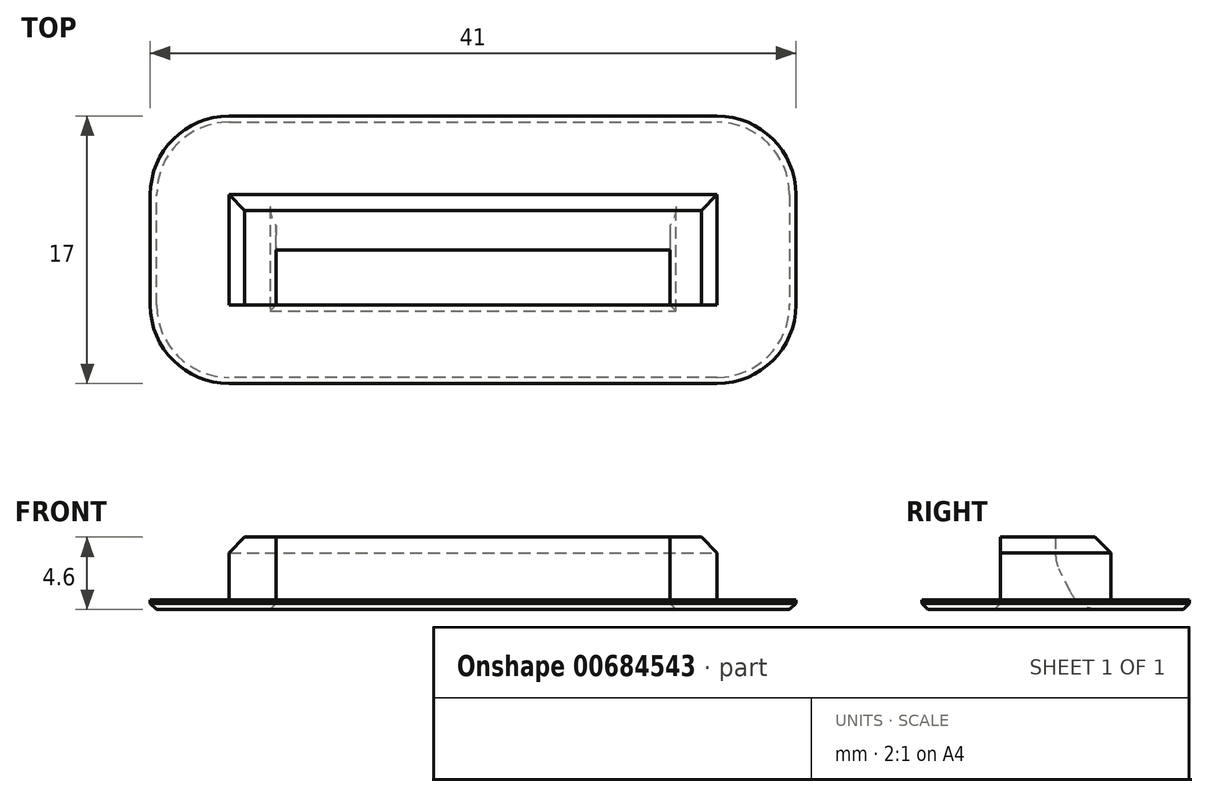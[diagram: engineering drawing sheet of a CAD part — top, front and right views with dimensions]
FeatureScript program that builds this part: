
annotation { "Feature Type Name" : "Feature", "Feature Type Description" : "" }
export const myFeature = defineFeature(function(context is Context, id is Id, definition is map)
    precondition{}
    {
        {
            var Q0;
            Q0=qCreatedBy(makeId("Top.planeOp"),FACE);
            var sketch = newSketch(context, id + "F0", { "sketchPlane" : qUnion([Q0])});
            skLineSegment(sketch, "E0.bottom", {"start": v(5, 0) * mm, "end": v(36, 0) * mm});
            skLineSegment(sketch, "E0.top", {"start": v(5, 17) * mm, "end": v(36, 17) * mm});
            skLineSegment(sketch, "E0.left", {"start": v(0, 5) * mm, "end": v(0, 12) * mm});
            skLineSegment(sketch, "E0.right", {"start": v(41, 5) * mm, "end": v(41, 12) * mm});
            skLineSegment(sketch, "E1.bottom", {"start": v(8, 0) * mm, "end": v(33, 0) * mm});
            skLineSegment(sketch, "E1.top", {"start": v(8, 8.5) * mm, "end": v(33, 8.5) * mm});
            skLineSegment(sketch, "E1.left", {"start": v(8, 0) * mm, "end": v(8, 8.5) * mm});
            skLineSegment(sketch, "E1.right", {"start": v(33, 0) * mm, "end": v(33, 8.5) * mm});
            skPoint(sketch, "E2.visualSharp", {"position": v(0, 17) * mm});
            skArc(sketch, "E2.filletArc", {"start": v(5, 17) * mm, "mid": v(1.46, 15.54) * mm, "end": v(0, 12) * mm});
            skPoint(sketch, "E3.visualSharp", {"position": v(0, 0) * mm});
            skArc(sketch, "E3.filletArc", {"start": v(0, 5) * mm, "mid": v(1.46, 1.46) * mm, "end": v(5, 0) * mm});
            skPoint(sketch, "E4.visualSharp", {"position": v(41, 17) * mm});
            skArc(sketch, "E4.filletArc", {"start": v(41, 12) * mm, "mid": v(39.54, 15.54) * mm, "end": v(36, 17) * mm});
            skPoint(sketch, "E5.visualSharp", {"position": v(41, 0) * mm});
            skArc(sketch, "E5.filletArc", {"start": v(36, 0) * mm, "mid": v(39.54, 1.46) * mm, "end": v(41, 5) * mm});
            skSolve(sketch);
        }
        {
            var Q0;
            Q0=makeQuery(id+"F0.imprint","IMPRINT",FACE,{"disambiguationData":[TD([[makeQuery(id+"F0.imprint","IMPRINT",EDGE,{"derivedFrom":sQuery(id+"F0.wireOp",EDGE,"E0.top")}),-1.0]])]});
            extrude(context, id + "F1", {"entities" : qUnion([Q0]), "depth" : 0.6 * mm, "offsetDistance" : 25 * mm});
        }
        {
            var Q0;
            Q0=makeQuery(id+"F1.opExtrude","CAP_FACE",FACE,{"disambiguationData":[OSD([sQuery(id+"F0.wireOp",EDGE,"E0.bottom"),sQuery(id+"F0.wireOp",EDGE,"E0.top"),sQuery(id+"F0.wireOp",EDGE,"E0.left"),sQuery(id+"F0.wireOp",EDGE,"E0.right"),sQuery(id+"F0.wireOp",EDGE,"E1.top"),sQuery(id+"F0.wireOp",EDGE,"E1.left"),sQuery(id+"F0.wireOp",EDGE,"E1.right"),sQuery(id+"F0.wireOp",EDGE,"E2.filletArc"),sQuery(id+"F0.wireOp",EDGE,"E3.filletArc"),sQuery(id+"F0.wireOp",EDGE,"E4.filletArc"),sQuery(id+"F0.wireOp",EDGE,"E5.filletArc")])],"isStart":false});
            var sketch = newSketch(context, id + "F2", { "sketchPlane" : qUnion([Q0])});
            skLineSegment(sketch, "E6.bottom", {"start": v(5, 12) * mm, "end": v(36, 12) * mm});
            skLineSegment(sketch, "E6.top", {"start": v(5, 5) * mm, "end": v(36, 5) * mm});
            skLineSegment(sketch, "E6.left", {"start": v(5, 12) * mm, "end": v(5, 5) * mm});
            skLineSegment(sketch, "E6.right", {"start": v(36, 12) * mm, "end": v(36, 5) * mm});
            skSolve(sketch);
        }
        {
            var Q0;
            Q0=makeQuery(id+"F2.imprint","IMPRINT",FACE,{"disambiguationData":[TD([[makeQuery(id+"F2.imprint","IMPRINT",EDGE,{"derivedFrom":sQuery(id+"F2.wireOp",EDGE,"E6.bottom")}),-1.0]])]});
            extrude(context, id + "F3", {"entities" : qUnion([Q0]), "operationType" : NewBodyOperationType.ADD, "depth" : 4 * mm, "offsetDistance" : 25 * mm});
        }
        {
            var Q0;
            Q0=makeQuery(id+"F3.opExtrude","CAP_EDGE",EDGE,{"disambiguationData":[OSD([sQuery(id+"F2.wireOp",EDGE,"E6.left")])],"isStart":false});
            var Q1;
            Q1=makeQuery(id+"F3.opExtrude","CAP_EDGE",EDGE,{"disambiguationData":[OSD([sQuery(id+"F2.wireOp",EDGE,"E6.bottom")])],"isStart":false});
            var Q2;
            Q2=makeQuery(id+"F3.opExtrude","CAP_EDGE",EDGE,{"disambiguationData":[OSD([sQuery(id+"F2.wireOp",EDGE,"E6.right")])],"isStart":false});
            chamfer(context, id + "F4", {"entities" : qUnion([Q0, Q1, Q2]), "width" : 1 * mm, "tangentPropagation" : true});
        }
        {
            var Q0;
            Q0=makeQuery(id+"F1.opExtrude","CAP_EDGE",EDGE,{"disambiguationData":[OSD([sQuery(id+"F0.wireOp",EDGE,"E1.top")])],"isStart":true});
            chamfer(context, id + "F5", {"entities" : qUnion([Q0]), "chamferType" : ChamferType.TWO_OFFSETS, "width1" : 3 * mm, "oppositeDirection" : false, "width2" : 1.5 * mm, "tangentPropagation" : true});
        }
        {
            var Q0;
            {var subQ0=sQuery(id+"F0.wireOp",EDGE,"E1.top");Q0=makeQuery(id+"F5.opChamfer","BLEND_EDGE",EDGE,{"blendedFrom":[makeQuery(id+"F1.opExtrude","CAP_EDGE",EDGE,{"disambiguationData":[OSD([subQ0])],"isStart":true}),makeQuery(id+"F1.opExtrude","CAP_FACE",FACE,{"disambiguationData":[OSD([sQuery(id+"F0.wireOp",EDGE,"E0.bottom"),sQuery(id+"F0.wireOp",EDGE,"E0.top"),sQuery(id+"F0.wireOp",EDGE,"E0.left"),sQuery(id+"F0.wireOp",EDGE,"E0.right"),subQ0,sQuery(id+"F0.wireOp",EDGE,"E1.left"),sQuery(id+"F0.wireOp",EDGE,"E1.right"),sQuery(id+"F0.wireOp",EDGE,"E2.filletArc"),sQuery(id+"F0.wireOp",EDGE,"E3.filletArc"),sQuery(id+"F0.wireOp",EDGE,"E4.filletArc"),sQuery(id+"F0.wireOp",EDGE,"E5.filletArc")])],"isStart":true})],"blendedInto":[makeQuery(id+"F1.opExtrude","CAP_FACE",FACE,{"disambiguationData":[OSD([sQuery(id+"F0.wireOp",EDGE,"E0.bottom"),sQuery(id+"F0.wireOp",EDGE,"E0.top"),sQuery(id+"F0.wireOp",EDGE,"E0.left"),sQuery(id+"F0.wireOp",EDGE,"E0.right"),subQ0,sQuery(id+"F0.wireOp",EDGE,"E1.left"),sQuery(id+"F0.wireOp",EDGE,"E1.right"),sQuery(id+"F0.wireOp",EDGE,"E2.filletArc"),sQuery(id+"F0.wireOp",EDGE,"E3.filletArc"),sQuery(id+"F0.wireOp",EDGE,"E4.filletArc"),sQuery(id+"F0.wireOp",EDGE,"E5.filletArc")])],"isStart":true})]});}
            var Q1;
            {var subQ0=sQuery(id+"F0.wireOp",EDGE,"E1.top");Q1=makeQuery(id+"F5.opChamfer","BLEND_EDGE",EDGE,{"blendedFrom":[makeQuery(id+"F1.opExtrude","CAP_EDGE",EDGE,{"disambiguationData":[OSD([subQ0])],"isStart":true}),makeQuery(id+"F3.boolean.opBoolean","MERGE",FACE,{"derivedFrom":[makeQuery(id+"F1.opExtrude","SWEPT_FACE",FACE,{"disambiguationData":[OSD([subQ0])]}),makeQuery(id+"F3.opExtrude","SWEPT_FACE",FACE,{"disambiguationData":[OSD([subQ0])]})]})],"blendedInto":[makeQuery(id+"F3.boolean.opBoolean","MERGE",FACE,{"derivedFrom":[makeQuery(id+"F1.opExtrude","SWEPT_FACE",FACE,{"disambiguationData":[OSD([subQ0])]}),makeQuery(id+"F3.opExtrude","SWEPT_FACE",FACE,{"disambiguationData":[OSD([subQ0])]})]})]});}
            fillet(context, id + "F6", {"entities" : qUnion([Q0, Q1]), "radius" : 2 * mm, "tangentPropagation" : true, "allowEdgeOverflow" : false});
        }
        {
            var Q0;
            {var subQ0=sQuery(id+"F0.wireOp",EDGE,"E1.left");Q0=makeQuery(id+"F3.boolean.opBoolean","MERGE",FACE,{"derivedFrom":[makeQuery(id+"F1.opExtrude","SWEPT_FACE",FACE,{"disambiguationData":[OSD([subQ0])]}),makeQuery(id+"F3.opExtrude","SWEPT_FACE",FACE,{"disambiguationData":[OSD([subQ0])]})]});}
            var sketch = newSketch(context, id + "F7", { "sketchPlane" : qUnion([Q0])});
            skLineSegment(sketch, "E7.bottom", {"start": v(5, 0.6) * mm, "end": v(0, 0.6) * mm});
            skLineSegment(sketch, "E7.top", {"start": v(5, 0) * mm, "end": v(0, 0) * mm});
            skLineSegment(sketch, "E7.left", {"start": v(5, 0.6) * mm, "end": v(5, 0) * mm});
            skLineSegment(sketch, "E7.right", {"start": v(0, 0.6) * mm, "end": v(0, 0) * mm});
            skSolve(sketch);
        }
        {
            var Q0;
            Q0=makeQuery(id+"F7.imprint","IMPRINT",FACE,{"disambiguationData":[TD([[makeQuery(id+"F7.imprint","IMPRINT",EDGE,{"derivedFrom":sQuery(id+"F7.wireOp",EDGE,"E7.bottom")}),-1.0]])]});
            extrude(context, id + "F8", {"entities" : qUnion([Q0]), "operationType" : NewBodyOperationType.ADD, "endBound" : BoundingType.UP_TO_NEXT, "depth" : 25 * mm, "offsetDistance" : 25 * mm});
        }
        {
            var Q0;
            Q0=makeQuery(id+"F1.opExtrude","CAP_EDGE",EDGE,{"disambiguationData":[OSD([sQuery(id+"F0.wireOp",EDGE,"E0.top")])],"isStart":true});
            var Q1;
            Q1=makeQuery(id+"F8.opExtrude","SWEPT_EDGE",EDGE,{"disambiguationData":[OSD([sQuery(id+"F0.wireOp",EDGE,"E1.left"),sQuery(id+"F7.wireOp",EDGE,"E7.top"),sQuery(id+"F7.wireOp",EDGE,"E7.left")])]});
            var Q2;
            Q2=makeQuery(id+"F1.opExtrude","CAP_EDGE",EDGE,{"disambiguationData":[OSD([sQuery(id+"F0.wireOp",EDGE,"E1.left")])],"isStart":true});
            var Q3;
            Q3=makeQuery(id+"F1.opExtrude","CAP_EDGE",EDGE,{"disambiguationData":[OSD([sQuery(id+"F0.wireOp",EDGE,"E1.right")])],"isStart":true});
            chamfer(context, id + "F9", {"entities" : qUnion([Q0, Q1, Q2, Q3]), "width" : 0.4 * mm, "tangentPropagation" : true});
        }
    });
